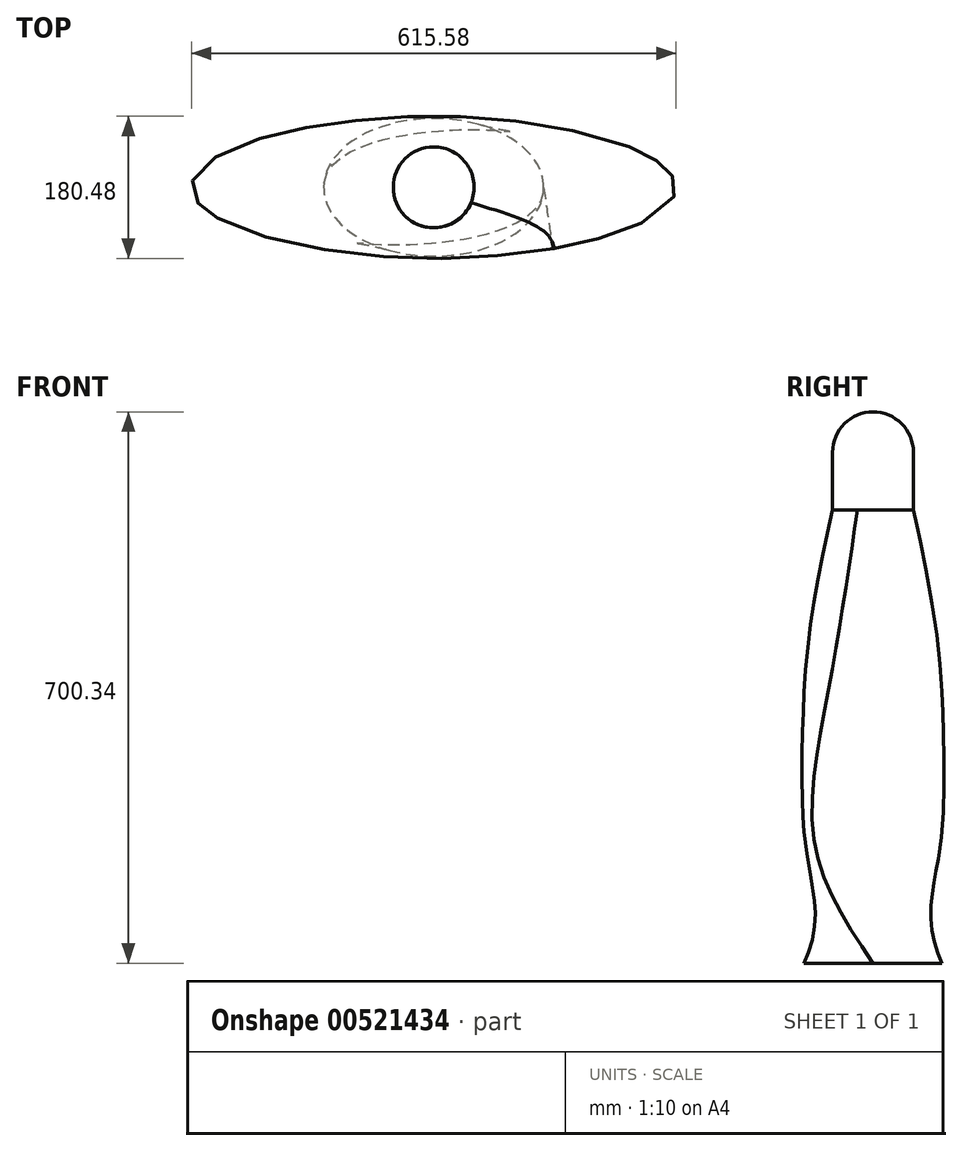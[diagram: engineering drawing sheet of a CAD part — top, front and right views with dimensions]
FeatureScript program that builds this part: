
annotation { "Feature Type Name" : "Feature", "Feature Type Description" : "" }
export const myFeature = defineFeature(function(context is Context, id is Id, definition is map)
    precondition{}
    {
        {
            var Q0;
            Q0=qCreatedBy(makeId("Top.planeOp"),FACE);
            cPlane(context, id + "F0", {"entities" : qUnion([Q0]), "cplaneType" : CPlaneType.OFFSET, "offset" : 159 * mm, "width" : 150 * mm, "height" : 150 * mm});
        }
        {
            var Q0;
            Q0=qCreatedBy(id+"F0.planeOp",FACE);
            cPlane(context, id + "F1", {"entities" : qUnion([Q0]), "cplaneType" : CPlaneType.OFFSET, "offset" : 171 * mm, "width" : 150 * mm, "height" : 150 * mm});
        }
        {
            var Q0;
            Q0=qCreatedBy(id+"F1.planeOp",FACE);
            cPlane(context, id + "F2", {"entities" : qUnion([Q0]), "cplaneType" : CPlaneType.OFFSET, "offset" : 246 * mm, "width" : 150 * mm, "height" : 150 * mm});
        }
        {
            var Q0;
            Q0=qCreatedBy(makeId("Top.planeOp"),FACE);
            var sketch = newSketch(context, id + "F3", { "sketchPlane" : qUnion([Q0])});
            skEllipse(sketch, "E0", {"center": v(0, 0) * mm, "majorRadius": 139.65 * mm, "minorRadius": 87.44 * mm, "majorAxis": v(1, 0)});
            skSolve(sketch);
        }
        {
            var Q0;
            Q0=qCreatedBy(id+"F0.planeOp",FACE);
            var sketch = newSketch(context, id + "F4", { "sketchPlane" : qUnion([Q0])});
            skEllipse(sketch, "E1", {"center": v(0, 0) * mm, "majorRadius": 307.16 * mm, "minorRadius": 86.6 * mm, "majorAxis": v(1, 0)});
            skSolve(sketch);
        }
        {
            var Q0;
            Q0=qCreatedBy(id+"F1.planeOp",FACE);
            var sketch = newSketch(context, id + "F5", { "sketchPlane" : qUnion([Q0])});
            skEllipse(sketch, "E2", {"center": v(0, 0) * mm, "majorRadius": 195.44 * mm, "minorRadius": 88.16 * mm, "majorAxis": v(1, 0)});
            skSolve(sketch);
        }
        {
            var Q0;
            Q0=qCreatedBy(id+"F2.planeOp",FACE);
            var sketch = newSketch(context, id + "F6", { "sketchPlane" : qUnion([Q0])});
            skCircle(sketch, "E3", {"center": v(0, 0) * mm, "radius": 51.34 * mm});
            skSolve(sketch);
        }
        {
            var Q0;
            Q0=makeQuery(id+"F3.imprint","IMPRINT",FACE,{"disambiguationData":[TD([[makeQuery(id+"F3.imprint","IMPRINT",EDGE,{"derivedFrom":sQuery(id+"F3.wireOp",EDGE,"E0")}),1.0]])]});
            var Q1;
            Q1=makeQuery(id+"F4.imprint","IMPRINT",FACE,{"disambiguationData":[TD([[makeQuery(id+"F4.imprint","IMPRINT",EDGE,{"derivedFrom":sQuery(id+"F4.wireOp",EDGE,"E1")}),1.0]])]});
            var Q2;
            Q2=makeQuery(id+"F5.imprint","IMPRINT",FACE,{"disambiguationData":[TD([[makeQuery(id+"F5.imprint","IMPRINT",EDGE,{"derivedFrom":sQuery(id+"F5.wireOp",EDGE,"E2")}),1.0]])]});
            var Q3;
            Q3=makeQuery(id+"F6.imprint","IMPRINT",FACE,{"disambiguationData":[TD([[makeQuery(id+"F6.imprint","IMPRINT",EDGE,{"derivedFrom":sQuery(id+"F6.wireOp",EDGE,"E3")}),1.0]])]});
            loft(context, id + "F7", {"sheetProfilesArray" : [{ "sheetProfileEntities" : qUnion([Q0]) }, { "sheetProfileEntities" : qUnion([Q1]) }, { "sheetProfileEntities" : qUnion([Q2]) }, { "sheetProfileEntities" : qUnion([Q3]) }]});
        }
        {
            var Q0;
            Q0=qCreatedBy(id+"F2.planeOp",FACE);
            var sketch = newSketch(context, id + "F8", { "sketchPlane" : qUnion([Q0])});
            skSolve(sketch);
        }
        {
            var Q0;
            Q0 = qSketchRegion(id + "F8", true);
            var Q1;
            Q1=makeQuery(id+"F7.opLoft","CAP_FACE",FACE,{"disambiguationData":[OSD([makeQuery(id+"F6.imprint","IMPRINT",FACE,{"disambiguationData":[TD([[makeQuery(id+"F6.imprint","IMPRINT",EDGE,{"derivedFrom":sQuery(id+"F6.wireOp",EDGE,"E3")}),1.0]])]})])],"isStart":true});
            extrude(context, id + "F9", {"entities" : qUnion([Q0, Q1]), "operationType" : NewBodyOperationType.ADD, "depth" : 73 * mm, "offsetDistance" : 25 * mm});
        }
        {
            var Q0;
            Q0=makeQuery(id+"F9.opExtrude","CAP_FACE",FACE,{"disambiguationData":[OSD([makeQuery(id+"F6.imprint","IMPRINT",FACE,{"disambiguationData":[TD([[makeQuery(id+"F6.imprint","IMPRINT",EDGE,{"derivedFrom":sQuery(id+"F6.wireOp",EDGE,"E3")}),1.0]])]})])],"isStart":false});
            var sketch = newSketch(context, id + "F10", { "sketchPlane" : qUnion([Q0])});
            skLineSegment(sketch, "E4", {"start": v(0, 51.34) * mm, "end": v(0, -51.34) * mm});
            skFitSpline(sketch, "E5.0", {"points": [v(47.43, -19.64) * mm, v(48.04, -18.16) * mm, v(48.61, -16.58) * mm, v(49.1, -14.97) * mm, v(49.13, -14.9) * mm, v(49.6, -13.37) * mm, v(50, -11.74) * mm, v(50.34, -10.1) * mm, v(50.35, -10) * mm, v(50.66, -8.44) * mm, v(50.91, -6.78) * mm, v(51.08, -5.1) * mm, v(51.1, -5.02) * mm, v(51.25, -3.44) * mm, v(51.33, -1.76) * mm, v(51.34, -0.08) * mm, v(51.34, 0.01) * mm, v(51.34, 1.6) * mm, v(51.26, 3.28) * mm, v(51.1, 4.96) * mm, v(51.09, 5.04) * mm, v(50.93, 6.63) * mm, v(50.69, 8.29) * mm, v(50.37, 9.94) * mm, v(50.35, 10.03) * mm, v(50.04, 11.59) * mm, v(49.63, 13.22) * mm, v(49.15, 14.83) * mm, v(49.12, 14.91) * mm, v(48.66, 16.44) * mm, v(48.1, 18.02) * mm, v(47.46, 19.57) * mm, v(47.42, 19.66) * mm, v(46.82, 21.13) * mm, v(46.1, 22.65) * mm, v(45.31, 24.13) * mm, v(45.27, 24.21) * mm, v(44.52, 25.61) * mm, v(43.66, 27.06) * mm, v(42.73, 28.46) * mm, v(42.68, 28.53) * mm, v(41.8, 29.85) * mm, v(40.8, 31.2) * mm, v(39.73, 32.5) * mm, v(39.68, 32.58) * mm, v(38.67, 33.8) * mm, v(37.54, 35.05) * mm, v(36.36, 36.25) * mm, v(36.3, 36.3) * mm, v(35.17, 37.43) * mm, v(33.92, 38.57) * mm, v(32.63, 39.64) * mm, v(32.56, 39.7) * mm, v(31.33, 40.7) * mm, v(29.98, 41.7) * mm, v(28.59, 42.64) * mm, v(28.51, 42.7) * mm, v(27.19, 43.58) * mm, v(25.75, 44.44) * mm, v(24.27, 45.24) * mm, v(24.2, 45.28) * mm, v(22.79, 46.03) * mm, v(21.27, 46.75) * mm, v(19.72, 47.4) * mm, v(19.64, 47.43) * mm, v(18.16, 48.04) * mm, v(16.58, 48.61) * mm, v(14.98, 49.1) * mm, v(14.9, 49.13) * mm, v(13.37, 49.6) * mm, v(11.74, 50) * mm, v(10.1, 50.34) * mm, v(10, 50.35) * mm, v(8.44, 50.66) * mm, v(6.78, 50.91) * mm, v(5.1, 51.08) * mm, v(5.02, 51.1) * mm, v(3.44, 51.25) * mm, v(1.76, 51.33) * mm, v(0.08, 51.34) * mm, v(-0.01, 51.34) * mm, v(-1.6, 51.34) * mm, v(-3.28, 51.26) * mm, v(-4.96, 51.1) * mm, v(-5.04, 51.09) * mm, v(-6.63, 50.93) * mm, v(-8.29, 50.69) * mm, v(-9.94, 50.37) * mm, v(-10.03, 50.35) * mm, v(-11.59, 50.04) * mm, v(-13.22, 49.63) * mm, v(-14.83, 49.15) * mm, v(-14.91, 49.12) * mm, v(-16.44, 48.66) * mm, v(-18.02, 48.1) * mm, v(-19.57, 47.46) * mm, v(-19.66, 47.42) * mm, v(-21.13, 46.82) * mm, v(-22.65, 46.1) * mm, v(-24.13, 45.31) * mm, v(-24.21, 45.27) * mm, v(-25.61, 44.52) * mm, v(-27.06, 43.66) * mm, v(-28.46, 42.73) * mm, v(-28.53, 42.68) * mm, v(-29.85, 41.8) * mm, v(-31.2, 40.8) * mm, v(-32.5, 39.73) * mm, v(-32.58, 39.68) * mm, v(-33.8, 38.67) * mm, v(-35.05, 37.54) * mm, v(-36.25, 36.36) * mm, v(-36.3, 36.3) * mm, v(-37.43, 35.17) * mm, v(-38.57, 33.92) * mm, v(-39.64, 32.63) * mm, v(-39.7, 32.56) * mm, v(-40.7, 31.33) * mm, v(-41.7, 29.98) * mm, v(-42.64, 28.59) * mm, v(-42.7, 28.51) * mm, v(-43.58, 27.19) * mm, v(-44.44, 25.75) * mm, v(-45.24, 24.27) * mm, v(-45.28, 24.2) * mm, v(-46.03, 22.79) * mm, v(-46.75, 21.27) * mm, v(-47.4, 19.72) * mm, v(-47.43, 19.64) * mm, v(-48.04, 18.16) * mm, v(-48.61, 16.58) * mm, v(-49.1, 14.98) * mm, v(-49.13, 14.9) * mm, v(-49.6, 13.37) * mm, v(-50, 11.74) * mm, v(-50.34, 10.1) * mm, v(-50.35, 10) * mm, v(-50.66, 8.44) * mm, v(-50.91, 6.78) * mm, v(-51.08, 5.1) * mm, v(-51.1, 5.02) * mm, v(-51.25, 3.44) * mm, v(-51.33, 1.76) * mm, v(-51.34, 0.08) * mm, v(-51.34, -0.01) * mm, v(-51.34, -1.6) * mm, v(-51.26, -3.28) * mm, v(-51.1, -4.96) * mm, v(-51.09, -5.04) * mm, v(-50.93, -6.63) * mm, v(-50.69, -8.29) * mm, v(-50.37, -9.94) * mm, v(-50.35, -10.03) * mm, v(-50.04, -11.59) * mm, v(-49.63, -13.22) * mm, v(-49.15, -14.83) * mm, v(-49.12, -14.91) * mm, v(-48.66, -16.44) * mm, v(-48.1, -18.02) * mm, v(-47.46, -19.57) * mm, v(-47.42, -19.66) * mm, v(-46.82, -21.13) * mm, v(-46.1, -22.65) * mm, v(-45.31, -24.13) * mm, v(-45.27, -24.21) * mm, v(-44.52, -25.61) * mm, v(-43.66, -27.06) * mm, v(-42.73, -28.46) * mm, v(-42.68, -28.53) * mm, v(-41.8, -29.85) * mm, v(-40.8, -31.2) * mm, v(-39.73, -32.5) * mm, v(-39.68, -32.58) * mm, v(-38.67, -33.8) * mm, v(-37.54, -35.05) * mm, v(-36.36, -36.25) * mm, v(-36.3, -36.3) * mm, v(-35.17, -37.43) * mm, v(-33.92, -38.57) * mm, v(-32.63, -39.64) * mm, v(-32.56, -39.7) * mm, v(-31.33, -40.7) * mm, v(-29.98, -41.7) * mm, v(-28.59, -42.64) * mm, v(-28.51, -42.7) * mm, v(-27.19, -43.58) * mm, v(-25.75, -44.44) * mm, v(-24.27, -45.24) * mm, v(-24.2, -45.28) * mm, v(-22.79, -46.03) * mm, v(-21.27, -46.75) * mm, v(-19.72, -47.4) * mm, v(-19.64, -47.43) * mm, v(-18.16, -48.04) * mm, v(-16.58, -48.61) * mm, v(-14.98, -49.1) * mm, v(-14.9, -49.13) * mm, v(-13.37, -49.6) * mm, v(-11.74, -50) * mm, v(-10.1, -50.34) * mm, v(-10, -50.35) * mm, v(-8.44, -50.66) * mm, v(-6.78, -50.91) * mm, v(-5.1, -51.08) * mm, v(-5.02, -51.1) * mm, v(-3.44, -51.25) * mm, v(-1.76, -51.33) * mm, v(-0.08, -51.34) * mm, v(0.01, -51.34) * mm, v(1.6, -51.34) * mm, v(3.28, -51.26) * mm, v(4.96, -51.1) * mm, v(5.04, -51.09) * mm, v(6.63, -50.93) * mm, v(8.29, -50.69) * mm, v(9.94, -50.37) * mm, v(10.03, -50.35) * mm, v(11.59, -50.04) * mm, v(13.22, -49.63) * mm, v(14.83, -49.15) * mm, v(14.91, -49.12) * mm, v(16.44, -48.66) * mm, v(18.02, -48.1) * mm, v(19.57, -47.46) * mm, v(19.66, -47.42) * mm, v(21.13, -46.82) * mm, v(22.65, -46.1) * mm, v(24.13, -45.31) * mm, v(24.21, -45.27) * mm, v(25.61, -44.52) * mm, v(27.06, -43.66) * mm, v(28.46, -42.73) * mm, v(28.53, -42.68) * mm, v(29.85, -41.8) * mm, v(31.2, -40.8) * mm, v(32.5, -39.73) * mm, v(32.58, -39.68) * mm, v(33.8, -38.67) * mm, v(35.05, -37.54) * mm, v(36.25, -36.36) * mm, v(36.3, -36.3) * mm, v(37.43, -35.17) * mm, v(38.57, -33.92) * mm, v(39.64, -32.63) * mm, v(39.7, -32.56) * mm, v(40.7, -31.33) * mm, v(41.7, -29.98) * mm, v(42.64, -28.59) * mm, v(42.7, -28.51) * mm, v(43.58, -27.19) * mm, v(44.44, -25.75) * mm, v(45.24, -24.27) * mm, v(45.28, -24.2) * mm, v(46.07, -22.7) * mm, v(46.8, -21.19) * mm, v(47.43, -19.64) * mm, v(47.43, -19.64) * mm]});
            skSolve(sketch);
        }
        {
            var Q0;
            {var subQ0=sQuery(id+"F10.wireOp",EDGE,"E4");Q0=makeQuery(id+"F10.imprint","IMPRINT",FACE,{"disambiguationData":[TD([[makeQuery(id+"F10.imprint","IMPRINT",EDGE,{"derivedFrom":subQ0}),1.0]])]});}
            var Q1;
            Q1=sQuery(id+"F10.wireOp",EDGE,"E4");
            revolve(context, id + "F11", {"operationType" : NewBodyOperationType.ADD, "entities" : qUnion([Q0]), "axis" : qUnion([Q1]), "revolveType" : RevolveType.FULL});
        }
    });
